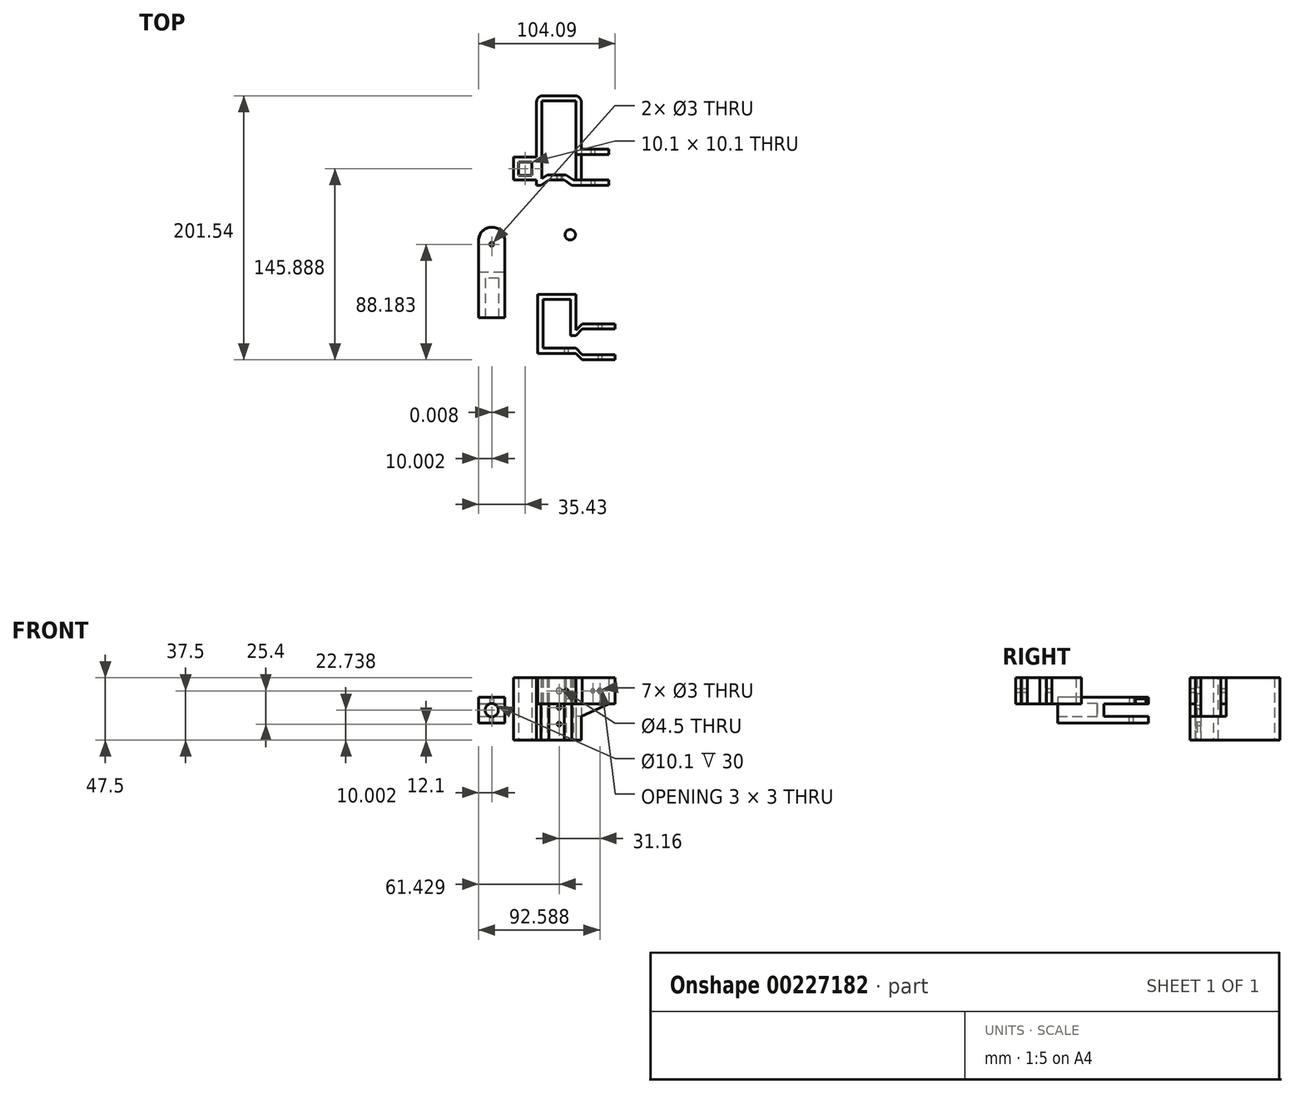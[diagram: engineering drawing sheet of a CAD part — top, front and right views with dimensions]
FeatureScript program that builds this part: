
annotation { "Feature Type Name" : "Feature", "Feature Type Description" : "" }
export const myFeature = defineFeature(function(context is Context, id is Id, definition is map)
    precondition{}
    {
        {
            var Q0;
            Q0=qCreatedBy(makeId("Top.planeOp"),FACE);
            var sketch = newSketch(context, id + "F0", { "sketchPlane" : qUnion([Q0])});
            skLineSegment(sketch, "E0.bottom", {"start": v(-21.91, 56.33) * mm, "end": v(-41.91, 56.33) * mm});
            skLineSegment(sketch, "E1", {"start": v(-21.93, 11.33) * mm, "end": v(-21.93, -13.67) * mm});
            skLineSegment(sketch, "E2.MirrorCS", {"start": v(-41.93, 11.33) * mm, "end": v(-41.93, -13.67) * mm});
            skLineSegment(sketch, "E3", {"start": v(-41.93, 11.33) * mm, "end": v(-21.93, 11.33) * mm});
            skLineSegment(sketch, "E4", {"start": v(-41.93, -13.67) * mm, "end": v(-21.93, -13.67) * mm});
            skLineSegment(sketch, "E5", {"start": v(-31.93, 11.33) * mm, "end": v(-31.91, 56.33) * mm});
            skCircle(sketch, "E6", {"center": v(-31.92, 32.33) * mm, "radius": 1.5 * mm});
            skLineSegment(sketch, "E7", {"start": v(-41.91, 56.33) * mm, "end": v(-41.93, 11.33) * mm});
            skLineSegment(sketch, "E8", {"start": v(-21.91, 56.33) * mm, "end": v(-21.93, 11.33) * mm});
            skLineSegment(sketch, "E9", {"start": v(-41.92, 45.34) * mm, "end": v(-21.92, 45.33) * mm});
            skLineSegment(sketch, "E10", {"start": v(7.2, -37.33) * mm, "end": v(32.2, -37.33) * mm});
            skLineSegment(sketch, "E11", {"start": v(32.2, -37.33) * mm, "end": v(37.16, -32.36) * mm});
            skLineSegment(sketch, "E12", {"start": v(37.16, -32.36) * mm, "end": v(62.16, -32.36) * mm});
            skLineSegment(sketch, "E13", {"start": v(62.16, -32.36) * mm, "end": v(62.16, -42.13) * mm});
            skLineSegment(sketch, "E14", {"start": v(7.2, -37.33) * mm, "end": v(7.2, -42.13) * mm});
            skLineSegment(sketch, "E15", {"start": v(7.2, -42.13) * mm, "end": v(62.16, -42.13) * mm, "construction": true});
            skLineSegment(sketch, "E16.MirrorCS", {"start": v(7.2, -46.93) * mm, "end": v(7.2, -42.13) * mm});
            skLineSegment(sketch, "E17.MirrorCS", {"start": v(7.2, -46.93) * mm, "end": v(32.2, -46.93) * mm});
            skLineSegment(sketch, "E18.MirrorCS", {"start": v(32.2, -46.93) * mm, "end": v(37.16, -51.89) * mm});
            skLineSegment(sketch, "E19.MirrorCS", {"start": v(37.16, -51.89) * mm, "end": v(62.16, -51.89) * mm});
            skLineSegment(sketch, "E20.MirrorCS", {"start": v(62.16, -51.89) * mm, "end": v(62.16, -42.13) * mm});
            skLineSegment(sketch, "E21", {"start": v(3.2, -42.13) * mm, "end": v(3.2, -33.36) * mm});
            skLineSegment(sketch, "E22", {"start": v(3.2, -33.36) * mm, "end": v(32.2, -33.36) * mm});
            skLineSegment(sketch, "E23", {"start": v(32.2, -33.36) * mm, "end": v(37.16, -28.4) * mm});
            skLineSegment(sketch, "E24.MirrorCS", {"start": v(3.2, -42.13) * mm, "end": v(3.2, -50.89) * mm});
            skLineSegment(sketch, "E25.MirrorCS", {"start": v(3.2, -50.89) * mm, "end": v(32.2, -50.89) * mm});
            skLineSegment(sketch, "E26.MirrorCS", {"start": v(32.2, -50.89) * mm, "end": v(37.16, -55.85) * mm});
            skLineSegment(sketch, "E27", {"start": v(62.16, -28.4) * mm, "end": v(62.16, -55.85) * mm});
            skLineSegment(sketch, "E28", {"start": v(37.16, -28.4) * mm, "end": v(62.16, -28.4) * mm});
            skLineSegment(sketch, "E29", {"start": v(37.16, -55.85) * mm, "end": v(62.16, -55.85) * mm});
            skLineSegment(sketch, "E30", {"start": v(3.2, -5.78) * mm, "end": v(3.2, -33.36) * mm});
            skLineSegment(sketch, "E31", {"start": v(7.2, -33.36) * mm, "end": v(7.2, -9.78) * mm});
            skLineSegment(sketch, "E32", {"start": v(7.2, -37.33) * mm, "end": v(7.2, -33.36) * mm});
            skLineSegment(sketch, "E33", {"start": v(32.2, -33.36) * mm, "end": v(32.2, -9.78) * mm});
            skLineSegment(sketch, "E34", {"start": v(28.2, -37.33) * mm, "end": v(28.2, -9.78) * mm});
            skLineSegment(sketch, "E35", {"start": v(7.2, -9.78) * mm, "end": v(32.2, -9.78) * mm});
            skLineSegment(sketch, "E36", {"start": v(32.2, -9.78) * mm, "end": v(32.2, -5.78) * mm});
            skLineSegment(sketch, "E37", {"start": v(3.2, -5.78) * mm, "end": v(32.2, -5.78) * mm});
            skLineSegment(sketch, "E38.MirrorCS", {"start": v(6.25, 85.29) * mm, "end": v(24.75, 85.29) * mm});
            skLineSegment(sketch, "E39", {"start": v(57.44, 104.81) * mm, "end": v(57.44, 77.29) * mm});
            skLineSegment(sketch, "E40", {"start": v(2.25, 81.29) * mm, "end": v(2.25, 145.69) * mm});
            skLineSegment(sketch, "E41", {"start": v(6.25, 85.29) * mm, "end": v(6.25, 141.69) * mm});
            skLineSegment(sketch, "E42", {"start": v(2.25, 81.29) * mm, "end": v(57.44, 81.29) * mm});
            skLineSegment(sketch, "E43", {"start": v(57.44, 77.29) * mm, "end": v(29.27, 77.29) * mm});
            skLineSegment(sketch, "E44", {"start": v(29.27, 77.29) * mm, "end": v(23.5, 81.29) * mm});
            skLineSegment(sketch, "E45", {"start": v(57.44, 91.05) * mm, "end": v(6.25, 91.05) * mm, "construction": true});
            skLineSegment(sketch, "E46", {"start": v(24.75, 85.29) * mm, "end": v(30.52, 81.29) * mm});
            skLineSegment(sketch, "E47", {"start": v(36.44, 104.81) * mm, "end": v(36.44, 145.69) * mm});
            skLineSegment(sketch, "E48", {"start": v(32.44, 100.81) * mm, "end": v(57.44, 100.81) * mm});
            skLineSegment(sketch, "E49", {"start": v(36.44, 104.81) * mm, "end": v(57.44, 104.81) * mm});
            skLineSegment(sketch, "E50", {"start": v(32.44, 100.81) * mm, "end": v(32.44, 141.69) * mm});
            skLineSegment(sketch, "E51", {"start": v(6.25, 141.69) * mm, "end": v(32.44, 141.69) * mm});
            skLineSegment(sketch, "E52", {"start": v(2.25, 145.69) * mm, "end": v(36.44, 145.69) * mm});
            skLineSegment(sketch, "E53", {"start": v(32.8, 81.29) * mm, "end": v(32.8, 77.29) * mm});
            skLineSegment(sketch, "E54", {"start": v(17.52, 85.29) * mm, "end": v(17.52, 81.29) * mm});
            skLineSegment(sketch, "E55.MirrorCS", {"start": v(10.3, 85.29) * mm, "end": v(4.53, 81.29) * mm});
            skLineSegment(sketch, "E56.MirrorCS", {"start": v(5.78, 77.29) * mm, "end": v(11.55, 81.29) * mm});
            skLineSegment(sketch, "E57.MirrorCS", {"start": v(2.25, 81.29) * mm, "end": v(2.25, 77.29) * mm});
            skLineSegment(sketch, "E58", {"start": v(5.78, 77.29) * mm, "end": v(2.25, 77.29) * mm});
            skLineSegment(sketch, "E59", {"start": v(6.25, 85.29) * mm, "end": v(6.25, 82.48) * mm});
            skSolve(sketch);
        }
        {
            var Q0;
            {var subQ2=sQuery(id+"F0.wireOp",EDGE,"CtE1QIkq-5tvS-lQmr-TLQE-PiAnWp6S8LlF");Q0=makeQuery(id+"F0.imprint","IMPRINT",FACE,{"disambiguationData":[TD([[makeQuery(id+"F0.imprint","IMPRINT",EDGE,{"derivedFrom":subQ2}),-1.0]])]});}
            var Q1;
            Q1=makeQuery(id+"F0.imprint","IMPRINT",FACE,{"disambiguationData":[TD([[makeQuery(id+"F0.imprint","IMPRINT",EDGE,{"derivedFrom":sQuery(id+"F0.wireOp",EDGE,"z6zBslmh-39Nm-7tGN-vX3i-qFsrJANIcQPB")}),-1.0]])]});
            var Q2;
            {var subQ2=sQuery(id+"F0.wireOp",EDGE,"9d48ba60-b61e-4945-9312-984ca757d42b0.MirrorCS");Q2=makeQuery(id+"F0.imprint","IMPRINT",FACE,{"disambiguationData":[TD([[makeQuery(id+"F0.imprint","IMPRINT",EDGE,{"derivedFrom":subQ2}),1.0]])]});}
            var Q3;
            {var subQ4=sQuery(id+"F0.wireOp",EDGE,"E1");Q3=makeQuery(id+"F0.imprint","IMPRINT",FACE,{"disambiguationData":[TD([[makeQuery(id+"F0.imprint","IMPRINT",EDGE,{"derivedFrom":subQ4}),-1.0]])]});}
            var Q4;
            {var subQ0=sQuery(id+"F0.wireOp",EDGE,"CtE1QIkq-5tvS-lQmr-TLQE-PiAnWp6S8LlF");Q4=makeQuery(id+"F0.imprint","IMPRINT",FACE,{"disambiguationData":[TD([[makeQuery(id+"F0.imprint","IMPRINT",EDGE,{"derivedFrom":subQ0}),1.0]])]});}
            var Q5;
            {var subQ4=sQuery(id+"F0.wireOp",EDGE,"daFnesJ6-epaf-a9xK-2GaG-miObHF0AM3f9");Q5=makeQuery(id+"F0.imprint","IMPRINT",FACE,{"disambiguationData":[TD([[makeQuery(id+"F0.imprint","IMPRINT",EDGE,{"derivedFrom":subQ4}),1.0]])]});}
            var Q6;
            {var subQ8=sQuery(id+"F0.wireOp",EDGE,"E8");var subQ10=makeQuery(id+"F0.imprint","IMPRINT",VERTEX,{"derivedFrom":subQ8});Q6=makeQuery(id+"F0.imprint","IMPRINT",FACE,{"disambiguationData":[TD([[makeQuery(id+"F0.imprint","IMPRINT",EDGE,{"disambiguationData":[TD([[subQ10,1.0]])],"derivedFrom":subQ8}),-1.0]])]});}
            var Q7;
            {var subQ10=sQuery(id+"F0.wireOp",EDGE,"c9a6f07b-14d8-4156-a2d3-0b1aa78cce260.MirrorCS");Q7=makeQuery(id+"F0.imprint","IMPRINT",FACE,{"disambiguationData":[TD([[makeQuery(id+"F0.imprint","IMPRINT",EDGE,{"derivedFrom":subQ10}),-1.0]])]});}
            var Q8;
            {var subQ1=sQuery(id+"F0.wireOp",EDGE,"E5");var subQ4=sQuery(id+"F0.wireOp",EDGE,"E3");var subQ5=makeQuery(id+"F0.imprint","INTERSECT",VERTEX,{"derivedFrom":[subQ4,subQ1]});Q8=makeQuery(id+"F0.imprint","IMPRINT",FACE,{"disambiguationData":[TD([[makeQuery(id+"F0.imprint","IMPRINT",EDGE,{"disambiguationData":[TD([[subQ5,-1.0]])],"derivedFrom":subQ1}),1.0]])]});}
            var Q9;
            {var subQ1=sQuery(id+"F0.wireOp",EDGE,"E5");var subQ6=sQuery(id+"F0.wireOp",EDGE,"E3");var subQ7=makeQuery(id+"F0.imprint","INTERSECT",VERTEX,{"derivedFrom":[subQ6,subQ1]});Q9=makeQuery(id+"F0.imprint","IMPRINT",FACE,{"disambiguationData":[TD([[makeQuery(id+"F0.imprint","IMPRINT",EDGE,{"disambiguationData":[TD([[subQ7,-1.0]])],"derivedFrom":subQ1}),-1.0]])]});}
            var Q10;
            Q10 = qSketchRegion(id + "F3", true);
            var Q11;
            Q11=makeQuery(id+"F0.imprint","IMPRINT",FACE,{"disambiguationData":[TD([[makeQuery(id+"F0.imprint","IMPRINT",EDGE,{"derivedFrom":sQuery(id+"F0.wireOp",EDGE,"1Q1dtNkS-BfXF-qmHB-TxVw-7IoFosjgP5cW.bottom")}),-1.0]])]});
            extrude(context, id + "F1", {"entities" : qUnion([Q0, Q1, Q2, Q3, Q4, Q5, Q6, Q7, Q8, Q9, Q10, Q11]), "depth" : 5 * mm, "offsetDistance" : 25 * mm});
        }
        {
            var Q0;
            Q0=makeQuery(id+"F1.opExtrude","SWEPT_EDGE",EDGE,{"disambiguationData":[OSD([sQuery(id+"F0.wireOp",EDGE,"E9"),sQuery(id+"F0.wireOp",EDGE,"c9a6f07b-14d8-4156-a2d3-0b1aa78cce260.MirrorCS")])]});
            var Q1;
            Q1=makeQuery(id+"F1.opExtrude","SWEPT_EDGE",EDGE,{"disambiguationData":[OSD([sQuery(id+"F0.wireOp",EDGE,"E8"),sQuery(id+"F0.wireOp",EDGE,"c9a6f07b-14d8-4156-a2d3-0b1aa78cce260.MirrorCS")])]});
            var Q2;
            Q2=makeQuery(id+"F1.opExtrude","SWEPT_EDGE",EDGE,{"disambiguationData":[OSD([sQuery(id+"F0.wireOp",EDGE,"E9"),sQuery(id+"F0.wireOp",EDGE,"daFnesJ6-epaf-a9xK-2GaG-miObHF0AM3f9")])]});
            var Q3;
            Q3=makeQuery(id+"F1.opExtrude","SWEPT_EDGE",EDGE,{"disambiguationData":[OSD([sQuery(id+"F0.wireOp",EDGE,"E7"),sQuery(id+"F0.wireOp",EDGE,"daFnesJ6-epaf-a9xK-2GaG-miObHF0AM3f9")])]});
            fillet(context, id + "F2", {"entities" : qUnion([Q0, Q1, Q2, Q3]), "radius" : 10 * mm, "tangentPropagation" : true, "allowEdgeOverflow" : false});
        }
        {
            var Q0;
            Q0=makeQuery(id+"F1.opExtrude","CAP_FACE",FACE,{"disambiguationData":[OSD([sQuery(id+"F0.wireOp",EDGE,"E0.bottom"),sQuery(id+"F0.wireOp",EDGE,"E1"),sQuery(id+"F0.wireOp",EDGE,"E2.MirrorCS"),sQuery(id+"F0.wireOp",EDGE,"E4"),sQuery(id+"F0.wireOp",EDGE,"E6"),sQuery(id+"F0.wireOp",EDGE,"E7"),sQuery(id+"F0.wireOp",EDGE,"E8")])],"isStart":true});
            var sketch = newSketch(context, id + "F3", { "sketchPlane" : qUnion([Q0])});
            skLineSegment(sketch, "E60", {"start": v(-41.93, -11.33) * mm, "end": v(-21.93, -11.33) * mm});
            skSolve(sketch);
        }
        {
            var Q0;
            Q0=makeQuery(id+"F3.imprint","IMPRINT",FACE,{"disambiguationData":[TD([[makeQuery(id+"F3.imprint","IMPRINT",EDGE,{"derivedFrom":sQuery(id+"F3.wireOp",EDGE,"E60")}),1.0]])]});
            extrude(context, id + "F4", {"entities" : qUnion([Q0]), "operationType" : NewBodyOperationType.ADD, "depth" : 9.53 * mm, "offsetDistance" : 25 * mm});
        }
        {
            var Q0;
            Q0=makeQuery(id+"F4.opExtrude","CAP_FACE",FACE,{"disambiguationData":[OSD([sQuery(id+"F0.wireOp",EDGE,"E1"),sQuery(id+"F0.wireOp",EDGE,"E2.MirrorCS"),sQuery(id+"F0.wireOp",EDGE,"E4"),sQuery(id+"F3.wireOp",EDGE,"E60")])],"isStart":false});
            var sketch = newSketch(context, id + "F5", { "sketchPlane" : qUnion([Q0])});
            skLineSegment(sketch, "E61.bottom", {"start": v(-21.93, 13.67) * mm, "end": v(-41.93, 13.67) * mm});
            skLineSegment(sketch, "E61.top", {"start": v(-21.93, -56.33) * mm, "end": v(-41.93, -56.33) * mm});
            skLineSegment(sketch, "E61.left", {"start": v(-21.93, 13.67) * mm, "end": v(-21.93, -56.33) * mm});
            skLineSegment(sketch, "E61.right", {"start": v(-41.93, 13.67) * mm, "end": v(-41.93, -56.33) * mm});
            skLineSegment(sketch, "E62", {"start": v(-21.93, -11.33) * mm, "end": v(-41.93, -11.33) * mm, "construction": true});
            skCircle(sketch, "E63", {"center": v(-31.93, -32.33) * mm, "radius": 1.5 * mm});
            skPoint(sketch, "E63.centerSnap0", {"position": v(-31.93, -11.33) * mm});
            skLineSegment(sketch, "E64", {"start": v(-21.93, -45.33) * mm, "end": v(-41.93, -45.33) * mm});
            skLineSegment(sketch, "E65", {"start": v(-31.93, -45.33) * mm, "end": v(-31.93, -11.33) * mm, "construction": true});
            skSolve(sketch);
        }
        {
            var Q0;
            {var subQ0=sQuery(id+"F5.wireOp",EDGE,"E61.bottom");Q0=makeQuery(id+"F5.imprint","IMPRINT",FACE,{"disambiguationData":[TD([[makeQuery(id+"F5.imprint","IMPRINT",EDGE,{"derivedFrom":subQ0}),1.0]])]});}
            var Q1;
            {var subQ0=sQuery(id+"F5.wireOp",EDGE,"E62");Q1=makeQuery(id+"F5.imprint","IMPRINT",FACE,{"disambiguationData":[TD([[makeQuery(id+"F5.imprint","IMPRINT",EDGE,{"derivedFrom":subQ0}),-1.0]])]});}
            var Q2;
            Q2=makeQuery(id+"F5.imprint","IMPRINT",FACE,{"disambiguationData":[TD([[makeQuery(id+"F5.imprint","IMPRINT",EDGE,{"derivedFrom":sQuery(id+"F5.wireOp",EDGE,"E63")}),-1.0]])]});
            var Q3;
            {var subQ0=sQuery(id+"F5.wireOp",EDGE,"E61.bottom");Q3=makeQuery(id+"F5.imprint","IMPRINT",FACE,{"disambiguationData":[TD([[makeQuery(id+"F5.imprint","IMPRINT",EDGE,{"derivedFrom":subQ0}),-1.0]])]});}
            extrude(context, id + "F6", {"entities" : qUnion([Q0, Q1, Q2, Q3]), "operationType" : NewBodyOperationType.ADD, "depth" : 5 * mm, "offsetDistance" : 25 * mm});
        }
        {
            var Q0;
            Q0=makeQuery(id+"F6.opExtrude","SWEPT_EDGE",EDGE,{"disambiguationData":[OSD([sQuery(id+"F5.wireOp",EDGE,"E61.right"),sQuery(id+"F5.wireOp",EDGE,"E64")])]});
            var Q1;
            Q1=makeQuery(id+"F6.opExtrude","SWEPT_EDGE",EDGE,{"disambiguationData":[OSD([sQuery(id+"F5.wireOp",EDGE,"E61.left"),sQuery(id+"F5.wireOp",EDGE,"E64")])]});
            fillet(context, id + "F7", {"entities" : qUnion([Q0, Q1]), "radius" : 10 * mm, "tangentPropagation" : true, "allowEdgeOverflow" : false});
        }
        {
            var Q0;
            {var subQ0=sQuery(id+"F0.wireOp",EDGE,"E4");Q0=makeQuery(id+"F4.boolean.opBoolean","MERGE",FACE,{"derivedFrom":[makeQuery(id+"F1.opExtrude","SWEPT_FACE",FACE,{"disambiguationData":[OSD([subQ0])]}),makeQuery(id+"F4.opExtrude","SWEPT_FACE",FACE,{"disambiguationData":[OSD([subQ0])]})]});}
            var sketch = newSketch(context, id + "F8", { "sketchPlane" : qUnion([Q0])});
            skCircle(sketch, "E66", {"center": v(-31.93, -4.76) * mm, "radius": 5.05 * mm});
            skPoint(sketch, "E66.centerSnap0", {"position": v(-31.93, 5) * mm});
            skSolve(sketch);
        }
        {
            var Q0;
            Q0=makeQuery(id+"F0.imprint","IMPRINT",FACE,{"disambiguationData":[TD([[makeQuery(id+"F0.imprint","IMPRINT",EDGE,{"derivedFrom":sQuery(id+"F0.wireOp",EDGE,"E14")}),-1.0]])]});
            var Q1;
            {var subQ0=sQuery(id+"F0.wireOp",EDGE,"E30");Q1=makeQuery(id+"F0.imprint","IMPRINT",FACE,{"disambiguationData":[TD([[makeQuery(id+"F0.imprint","IMPRINT",EDGE,{"derivedFrom":subQ0}),1.0]])]});}
            var Q2;
            {var subQ0=sQuery(id+"F0.wireOp",EDGE,"E12");Q2=makeQuery(id+"F0.imprint","IMPRINT",FACE,{"disambiguationData":[TD([[makeQuery(id+"F0.imprint","IMPRINT",EDGE,{"derivedFrom":subQ0}),1.0]])]});}
            var Q3;
            {var subQ3=sQuery(id+"F0.wireOp",EDGE,"XBbEQiE6-Z9xt-ZPnH-mPWf-PrI6pPlz04wO");Q3=makeQuery(id+"F0.imprint","IMPRINT",FACE,{"disambiguationData":[TD([[makeQuery(id+"F0.imprint","IMPRINT",EDGE,{"derivedFrom":subQ3}),-1.0]])]});}
            var Q4;
            {var subQ0=sQuery(id+"F0.wireOp",EDGE,"E33");Q4=makeQuery(id+"F0.imprint","IMPRINT",FACE,{"disambiguationData":[TD([[makeQuery(id+"F0.imprint","IMPRINT",EDGE,{"derivedFrom":subQ0}),1.0]])]});}
            var Q5;
            {var subQ1=sQuery(id+"F0.wireOp",EDGE,"72db4730-2340-4a1c-bc84-b23054559dcc");Q5=makeQuery(id+"F0.imprint","IMPRINT",FACE,{"disambiguationData":[TD([[makeQuery(id+"F0.imprint","IMPRINT",EDGE,{"derivedFrom":subQ1}),1.0]])]});}
            var Q6;
            Q6=makeQuery(id+"F0.imprint","IMPRINT",FACE,{"disambiguationData":[TD([[makeQuery(id+"F0.imprint","IMPRINT",EDGE,{"derivedFrom":sQuery(id+"F0.wireOp",EDGE,"d60c7e22-afe8-4185-99c7-5cb7434f99d0")}),-1.0]])]});
            var Q7;
            {var subQ0=sQuery(id+"F0.wireOp",EDGE,"E43");Q7=makeQuery(id+"F0.imprint","IMPRINT",FACE,{"disambiguationData":[TD([[makeQuery(id+"F0.imprint","IMPRINT",EDGE,{"derivedFrom":subQ0}),-1.0]])]});}
            var Q8;
            {var subQ0=sQuery(id+"F0.wireOp",EDGE,"CSoZNY7o-y4bp-1TmG-7ssV-1xZfQapDGbnf");Q8=makeQuery(id+"F0.imprint","IMPRINT",FACE,{"disambiguationData":[TD([[makeQuery(id+"F0.imprint","IMPRINT",EDGE,{"derivedFrom":subQ0}),-1.0]])]});}
            var Q9;
            {var subQ3=sQuery(id+"F0.wireOp",EDGE,"uGOKfyWa-nkCR-v7qt-ErlA-4CgWz3QyV5Tk");Q9=makeQuery(id+"F0.imprint","IMPRINT",FACE,{"disambiguationData":[TD([[makeQuery(id+"F0.imprint","IMPRINT",EDGE,{"derivedFrom":subQ3}),1.0]])]});}
            var Q10;
            {var subQ0=sQuery(id+"F0.wireOp",EDGE,"E44");Q10=makeQuery(id+"F0.imprint","IMPRINT",FACE,{"disambiguationData":[TD([[makeQuery(id+"F0.imprint","IMPRINT",EDGE,{"derivedFrom":subQ0}),-1.0]])]});}
            var Q11;
            {var subQ2=sQuery(id+"F0.wireOp",EDGE,"E40");Q11=makeQuery(id+"F0.imprint","IMPRINT",FACE,{"disambiguationData":[TD([[makeQuery(id+"F0.imprint","IMPRINT",EDGE,{"derivedFrom":subQ2}),-1.0]])]});}
            var Q12;
            {var subQ2=sQuery(id+"F0.wireOp",EDGE,"8fHTCkTu-zAOj-TMkr-ZO5F-SEi9VVDEdafV");Q12=makeQuery(id+"F0.imprint","IMPRINT",FACE,{"disambiguationData":[TD([[makeQuery(id+"F0.imprint","IMPRINT",EDGE,{"derivedFrom":subQ2}),-1.0]])]});}
            var Q13;
            {var subQ3=sQuery(id+"F0.wireOp",EDGE,"E56.MirrorCS");Q13=makeQuery(id+"F0.imprint","IMPRINT",FACE,{"disambiguationData":[TD([[makeQuery(id+"F0.imprint","IMPRINT",EDGE,{"derivedFrom":subQ3}),1.0]])]});}
            var Q14;
            {var subQ0=sQuery(id+"F0.wireOp",EDGE,"E54");Q14=makeQuery(id+"F0.imprint","IMPRINT",FACE,{"disambiguationData":[TD([[makeQuery(id+"F0.imprint","IMPRINT",EDGE,{"derivedFrom":subQ0}),-1.0]])]});}
            var Q15;
            {var subQ0=sQuery(id+"F0.wireOp",EDGE,"E46");Q15=makeQuery(id+"F0.imprint","IMPRINT",FACE,{"disambiguationData":[TD([[makeQuery(id+"F0.imprint","IMPRINT",EDGE,{"derivedFrom":subQ0}),-1.0]])]});}
            extrude(context, id + "F9", {"entities" : qUnion([Q0, Q1, Q2, Q3, Q4, Q5, Q6, Q7, Q8, Q9, Q10, Q11, Q12, Q13, Q14, Q15]), "depth" : 20 * mm, "offsetDistance" : 25 * mm});
        }
        {
            var Q0;
            Q0=makeQuery(id+"F9.opExtrude","SWEPT_FACE",FACE,{"disambiguationData":[OSD([sQuery(id+"F0.wireOp",EDGE,"E29")])]});
            var sketch = newSketch(context, id + "F10", { "sketchPlane" : qUnion([Q0])});
            skCircle(sketch, "E67", {"center": v(50.66, 10) * mm, "radius": 1.5 * mm});
            skPoint(sketch, "E67.centerSnap0", {"position": v(37.16, 10) * mm});
            skSolve(sketch);
        }
        {
            var Q0;
            Q0=makeQuery(id+"F9.opExtrude","SWEPT_FACE",FACE,{"disambiguationData":[OSD([sQuery(id+"F0.wireOp",EDGE,"E25.MirrorCS")])]});
            var sketch = newSketch(context, id + "F11", { "sketchPlane" : qUnion([Q0])});
            skPoint(sketch, "E68.centerSnap0", {"position": v(32.2, 10) * mm});
            skPoint(sketch, "E68.centerSnap1", {"position": v(17.7, 20) * mm});
            skCircle(sketch, "E69", {"center": v(24.9, 10) * mm, "radius": 1.5 * mm});
            skSolve(sketch);
        }
        {
            var Q0;
            Q0=makeQuery(id+"F11.imprint","IMPRINT",FACE,{"disambiguationData":[TD([[makeQuery(id+"F11.imprint","IMPRINT",EDGE,{"derivedFrom":sQuery(id+"F11.wireOp",EDGE,"E68")}),1.0]])]});
            var Q1;
            Q1=makeQuery(id+"F11.imprint","IMPRINT",FACE,{"disambiguationData":[TD([[makeQuery(id+"F11.imprint","IMPRINT",EDGE,{"derivedFrom":sQuery(id+"F11.wireOp",EDGE,"E69")}),1.0]])]});
            extrude(context, id + "F12", {"entities" : qUnion([Q0, Q1]), "operationType" : NewBodyOperationType.REMOVE, "oppositeDirection" : true, "depth" : 25 * mm, "offsetDistance" : 25 * mm});
        }
        {
            var Q0;
            Q0=makeQuery(id+"F10.imprint","IMPRINT",FACE,{"disambiguationData":[TD([[makeQuery(id+"F10.imprint","IMPRINT",EDGE,{"derivedFrom":sQuery(id+"F10.wireOp",EDGE,"Pd4Yzp6c-uVQW-pqn9-VgG2-u9d980DHV2Mr")}),1.0]])]});
            var Q1;
            Q1=makeQuery(id+"F10.imprint","IMPRINT",FACE,{"disambiguationData":[TD([[makeQuery(id+"F10.imprint","IMPRINT",EDGE,{"derivedFrom":sQuery(id+"F10.wireOp",EDGE,"ebFhJDeN-R1jm-PNRe-eJwy-XtfoPDOoVAFP")}),1.0]])]});
            var Q2;
            Q2=makeQuery(id+"F10.imprint","IMPRINT",FACE,{"disambiguationData":[TD([[makeQuery(id+"F10.imprint","IMPRINT",EDGE,{"derivedFrom":sQuery(id+"F10.wireOp",EDGE,"E67")}),1.0]])]});
            extrude(context, id + "F13", {"entities" : qUnion([Q0, Q1, Q2]), "operationType" : NewBodyOperationType.REMOVE, "oppositeDirection" : true, "depth" : 35 * mm, "offsetDistance" : 25 * mm});
        }
        {
            var Q0;
            Q0=makeQuery(id+"F8.imprint","IMPRINT",FACE,{"disambiguationData":[TD([[makeQuery(id+"F8.imprint","IMPRINT",EDGE,{"derivedFrom":sQuery(id+"F8.wireOp",EDGE,"E66")}),1.0]])]});
            extrude(context, id + "F14", {"entities" : qUnion([Q0]), "operationType" : NewBodyOperationType.REMOVE, "oppositeDirection" : true, "depth" : 20 * mm, "offsetDistance" : 25 * mm});
        }
        {
            var Q0;
            {var subQ0=sQuery(id+"F0.wireOp",EDGE,"E42");Q0=makeQuery(id+"F9.opExtrude","SWEPT_FACE",FACE,{"disambiguationData":[OSD([subQ0]),TDD([makeQuery(id+"F0.imprint","IMPRINT",EDGE,{"disambiguationData":[TD([[makeQuery(id+"F0.imprint","INTERSECT",VERTEX,{"derivedFrom":[subQ0,sQuery(id+"F0.wireOp",EDGE,"E44")]}),1.0]])],"derivedFrom":subQ0})])]});}
            var sketch = newSketch(context, id + "F15", { "sketchPlane" : qUnion([Q0])});
            skCircle(sketch, "E70", {"center": v(19.5, 10) * mm, "radius": 2.25 * mm});
            skCircle(sketch, "E71", {"center": v(19.5, -2.7) * mm, "radius": 1.5 * mm});
            skCircle(sketch, "E72", {"center": v(19.5, -15.4) * mm, "radius": 1.5 * mm});
            skSolve(sketch);
        }
        {
            var Q0;
            Q0=makeQuery(id+"F15.imprint","IMPRINT",FACE,{"disambiguationData":[TD([[makeQuery(id+"F15.imprint","IMPRINT",EDGE,{"derivedFrom":sQuery(id+"F15.wireOp",EDGE,"E72")}),1.0]])]});
            var Q1;
            Q1=makeQuery(id+"F15.imprint","IMPRINT",FACE,{"disambiguationData":[TD([[makeQuery(id+"F15.imprint","IMPRINT",EDGE,{"derivedFrom":sQuery(id+"F15.wireOp",EDGE,"E71")}),1.0]])]});
            var Q2;
            Q2=makeQuery(id+"F15.imprint","IMPRINT",FACE,{"disambiguationData":[TD([[makeQuery(id+"F15.imprint","IMPRINT",EDGE,{"derivedFrom":sQuery(id+"F15.wireOp",EDGE,"E70")}),1.0]])]});
            extrude(context, id + "F16", {"entities" : qUnion([Q0, Q1, Q2]), "operationType" : NewBodyOperationType.REMOVE, "oppositeDirection" : true, "depth" : 25 * mm, "offsetDistance" : 25 * mm});
        }
        {
            var Q0;
            Q0=makeQuery(id+"F9.opExtrude","SWEPT_FACE",FACE,{"disambiguationData":[OSD([sQuery(id+"F0.wireOp",EDGE,"E43")])]});
            var sketch = newSketch(context, id + "F17", { "sketchPlane" : qUnion([Q0])});
            skCircle(sketch, "E73", {"center": v(45.19, 10) * mm, "radius": 1.5 * mm});
            skSolve(sketch);
        }
        {
            var Q0;
            Q0 = qSketchRegion(id + "F17", true);
            extrude(context, id + "F18", {"entities" : qUnion([Q0]), "operationType" : NewBodyOperationType.REMOVE, "oppositeDirection" : true, "depth" : 35 * mm, "offsetDistance" : 25 * mm});
        }
        {
            var Q0;
            {var subQ0=sQuery(id+"F0.wireOp",EDGE,"E44");Q0=makeQuery(id+"F0.imprint","IMPRINT",FACE,{"disambiguationData":[TD([[makeQuery(id+"F0.imprint","IMPRINT",EDGE,{"derivedFrom":subQ0}),-1.0]])]});}
            var Q1;
            {var subQ2=sQuery(id+"F0.wireOp",EDGE,"8fHTCkTu-zAOj-TMkr-ZO5F-SEi9VVDEdafV");Q1=makeQuery(id+"F0.imprint","IMPRINT",FACE,{"disambiguationData":[TD([[makeQuery(id+"F0.imprint","IMPRINT",EDGE,{"derivedFrom":subQ2}),-1.0]])]});}
            var Q2;
            {var subQ0=sQuery(id+"F0.wireOp",EDGE,"E54");Q2=makeQuery(id+"F0.imprint","IMPRINT",FACE,{"disambiguationData":[TD([[makeQuery(id+"F0.imprint","IMPRINT",EDGE,{"derivedFrom":subQ0}),-1.0]])]});}
            var Q3;
            {var subQ0=sQuery(id+"F0.wireOp",EDGE,"E46");Q3=makeQuery(id+"F0.imprint","IMPRINT",FACE,{"disambiguationData":[TD([[makeQuery(id+"F0.imprint","IMPRINT",EDGE,{"derivedFrom":subQ0}),-1.0]])]});}
            var Q4;
            {var subQ4=sQuery(id+"F0.wireOp",EDGE,"E40");Q4=makeQuery(id+"F0.imprint","IMPRINT",FACE,{"disambiguationData":[TD([[makeQuery(id+"F0.imprint","IMPRINT",EDGE,{"derivedFrom":subQ4}),-1.0]])]});}
            var Q5;
            {var subQ3=sQuery(id+"F0.wireOp",EDGE,"E56.MirrorCS");Q5=makeQuery(id+"F0.imprint","IMPRINT",FACE,{"disambiguationData":[TD([[makeQuery(id+"F0.imprint","IMPRINT",EDGE,{"derivedFrom":subQ3}),1.0]])]});}
            extrude(context, id + "F19", {"entities" : qUnion([Q0, Q1, Q2, Q3, Q4, Q5]), "operationType" : NewBodyOperationType.ADD, "oppositeDirection" : true, "depth" : 27.5 * mm, "offsetDistance" : 25 * mm});
        }
        {
            var Q0;
            {var subQ0=sQuery(id+"F0.wireOp",EDGE,"E48");Q0=makeQuery(id+"F19.boolean.opBoolean","MERGE",FACE,{"derivedFrom":[makeQuery(id+"F9.opExtrude","SWEPT_FACE",FACE,{"disambiguationData":[OSD([subQ0])]}),makeQuery(id+"F19.opExtrude","SWEPT_FACE",FACE,{"disambiguationData":[OSD([subQ0])]})]});}
            var sketch = newSketch(context, id + "F20", { "sketchPlane" : qUnion([Q0])});
            skLineSegment(sketch, "E74", {"start": v(36.44, -27.5) * mm, "end": v(36.44, -9.5) * mm});
            skLineSegment(sketch, "E75", {"start": v(36.44, -9.5) * mm, "end": v(32.44, -9.5) * mm});
            skSolve(sketch);
        }
        {
            var Q0;
            {var subQ0=sQuery(id+"F20.wireOp",EDGE,"E74");Q0=makeQuery(id+"F20.imprint","IMPRINT",FACE,{"disambiguationData":[TD([[makeQuery(id+"F20.imprint","IMPRINT",EDGE,{"derivedFrom":subQ0}),1.0]])]});}
            extrude(context, id + "F21", {"entities" : qUnion([Q0]), "operationType" : NewBodyOperationType.ADD, "depth" : 23.52 * mm, "offsetDistance" : 25 * mm});
        }
        {
            var Q0;
            Q0=makeQuery(id+"F15.imprint","IMPRINT",FACE,{"disambiguationData":[TD([[makeQuery(id+"F15.imprint","IMPRINT",EDGE,{"derivedFrom":sQuery(id+"F15.wireOp",EDGE,"E72")}),1.0]])]});
            var Q1;
            Q1=makeQuery(id+"F15.imprint","IMPRINT",FACE,{"disambiguationData":[TD([[makeQuery(id+"F15.imprint","IMPRINT",EDGE,{"derivedFrom":sQuery(id+"F15.wireOp",EDGE,"E71")}),1.0]])]});
            extrude(context, id + "F22", {"entities" : qUnion([Q0, Q1]), "operationType" : NewBodyOperationType.REMOVE, "oppositeDirection" : true, "depth" : 25 * mm, "offsetDistance" : 25 * mm});
        }
        {
            var Q0;
            {var subQ0=sQuery(id+"F0.wireOp",EDGE,"E43");Q0=makeQuery(id+"F21.boolean.opBoolean","MERGE",FACE,{"derivedFrom":[makeQuery(id+"F19.boolean.opBoolean","MERGE",FACE,{"derivedFrom":[makeQuery(id+"F9.opExtrude","SWEPT_FACE",FACE,{"disambiguationData":[OSD([subQ0])]}),makeQuery(id+"F19.opExtrude","SWEPT_FACE",FACE,{"disambiguationData":[OSD([subQ0])]})]}),makeQuery(id+"F21.opExtrude","CAP_FACE",FACE,{"disambiguationData":[OSD([sQuery(id+"F0.wireOp",EDGE,"E48"),sQuery(id+"F0.wireOp",EDGE,"E50"),sQuery(id+"F20.wireOp",EDGE,"E74"),sQuery(id+"F20.wireOp",EDGE,"E75")])],"isStart":false})]});}
            var sketch = newSketch(context, id + "F23", { "sketchPlane" : qUnion([Q0])});
            skLineSegment(sketch, "E76", {"start": v(36.44, -9.5) * mm, "end": v(57.44, 0) * mm});
            skLineSegment(sketch, "E77", {"start": v(36.44, -27.5) * mm, "end": v(57.44, -27.5) * mm});
            skLineSegment(sketch, "E78", {"start": v(57.44, -27.5) * mm, "end": v(57.44, 0) * mm});
            skSolve(sketch);
        }
        {
            var Q0;
            Q0=makeQuery(id+"F23.imprint","IMPRINT",FACE,{"disambiguationData":[TD([[makeQuery(id+"F23.imprint","IMPRINT",EDGE,{"derivedFrom":sQuery(id+"F23.wireOp",EDGE,"E76")}),1.0]])]});
            extrude(context, id + "F24", {"entities" : qUnion([Q0]), "operationType" : NewBodyOperationType.ADD, "oppositeDirection" : true, "depth" : 4 * mm, "offsetDistance" : 25 * mm});
        }
        {
            var Q0;
            Q0=makeQuery(id+"F23.imprint","IMPRINT",FACE,{"disambiguationData":[TD([[makeQuery(id+"F23.imprint","IMPRINT",EDGE,{"derivedFrom":sQuery(id+"F23.wireOp",EDGE,"E76")}),-1.0]])]});
            extrude(context, id + "F25", {"entities" : qUnion([Q0]), "operationType" : NewBodyOperationType.REMOVE, "oppositeDirection" : true, "depth" : 35 * mm, "offsetDistance" : 25 * mm});
        }
        {
            var Q0;
            {var subQ0=sQuery(id+"F0.wireOp",EDGE,"E52");var subQ1=sQuery(id+"F0.wireOp",EDGE,"E40");Q0=makeQuery(id+"F19.boolean.opBoolean","MERGE",EDGE,{"derivedFrom":[makeQuery(id+"F9.opExtrude","SWEPT_EDGE",EDGE,{"disambiguationData":[OSD([subQ1,subQ0])]}),makeQuery(id+"F19.opExtrude","SWEPT_EDGE",EDGE,{"disambiguationData":[OSD([subQ1,subQ0])]})]});}
            var Q1;
            {var subQ0=sQuery(id+"F0.wireOp",EDGE,"E52");var subQ1=sQuery(id+"F0.wireOp",EDGE,"E47");Q1=makeQuery(id+"F19.boolean.opBoolean","MERGE",EDGE,{"derivedFrom":[makeQuery(id+"F9.opExtrude","SWEPT_EDGE",EDGE,{"disambiguationData":[OSD([subQ1,subQ0])]}),makeQuery(id+"F19.opExtrude","SWEPT_EDGE",EDGE,{"disambiguationData":[OSD([subQ1,subQ0])]})]});}
            fillet(context, id + "F26", {"entities" : qUnion([Q0, Q1]), "radius" : 5 * mm, "tangentPropagation" : true, "allowEdgeOverflow" : false});
        }
        {
            var Q0;
            {var subQ0=sQuery(id+"F0.wireOp",EDGE,"E40");Q0=makeQuery(id+"F19.boolean.opBoolean","MERGE",FACE,{"derivedFrom":[makeQuery(id+"F9.opExtrude","SWEPT_FACE",FACE,{"disambiguationData":[OSD([subQ0])]}),makeQuery(id+"F19.opExtrude","SWEPT_FACE",FACE,{"disambiguationData":[OSD([subQ0])]})]});}
            var sketch = newSketch(context, id + "F27", { "sketchPlane" : qUnion([Q0])});
            skLineSegment(sketch, "E79", {"start": v(-81.29, -27.5) * mm, "end": v(-98.79, -27.5) * mm});
            skLineSegment(sketch, "E80", {"start": v(-98.79, -27.5) * mm, "end": v(-98.79, 20) * mm});
            skLineSegment(sketch, "E81", {"start": v(-98.79, 20) * mm, "end": v(-81.29, 20) * mm});
            skLineSegment(sketch, "E82", {"start": v(-81.29, 20) * mm, "end": v(-81.29, -27.5) * mm});
            skSolve(sketch);
        }
        {
            var Q0;
            Q0=makeQuery(id+"F27.imprint","IMPRINT",FACE,{"disambiguationData":[TD([[makeQuery(id+"F27.imprint","IMPRINT",EDGE,{"derivedFrom":sQuery(id+"F27.wireOp",EDGE,"E79")}),-1.0]])]});
            extrude(context, id + "F28", {"entities" : qUnion([Q0]), "operationType" : NewBodyOperationType.ADD, "depth" : 17.5 * mm, "offsetDistance" : 25 * mm});
        }
        {
            var Q0;
            Q0=makeQuery(id+"F28.opExtrude","SWEPT_FACE",FACE,{"disambiguationData":[OSD([sQuery(id+"F27.wireOp",EDGE,"E79")])]});
            var sketch = newSketch(context, id + "F29", { "sketchPlane" : qUnion([Q0])});
            skLineSegment(sketch, "E83.bottom", {"start": v(-11.55, -84.99) * mm, "end": v(-1.45, -84.99) * mm});
            skLineSegment(sketch, "E83.top", {"start": v(-11.55, -95.09) * mm, "end": v(-1.45, -95.09) * mm});
            skLineSegment(sketch, "E83.left", {"start": v(-11.55, -84.99) * mm, "end": v(-11.55, -95.09) * mm});
            skLineSegment(sketch, "E83.right", {"start": v(-1.45, -84.99) * mm, "end": v(-1.45, -95.09) * mm});
            skPoint(sketch, "E83.middle", {"position": v(-6.5, -90.04) * mm});
            skPoint(sketch, "E83.middle.positionSnap0", {"position": v(-6.5, -98.79) * mm});
            skPoint(sketch, "E83.middle.positionSnap1", {"position": v(-15.25, -90.04) * mm});
            skPoint(sketch, "E83.centerSnap0", {"position": v(-6.5, -98.79) * mm});
            skPoint(sketch, "E83.centerSnap1", {"position": v(-15.25, -90.04) * mm});
            skSolve(sketch);
        }
        {
            var Q0;
            Q0=makeQuery(id+"F29.imprint","IMPRINT",FACE,{"disambiguationData":[TD([[makeQuery(id+"F29.imprint","IMPRINT",EDGE,{"derivedFrom":sQuery(id+"F29.wireOp",EDGE,"E83.bottom")}),-1.0]])]});
            extrude(context, id + "F30", {"entities" : qUnion([Q0]), "operationType" : NewBodyOperationType.REMOVE, "oppositeDirection" : true, "depth" : 50 * mm, "offsetDistance" : 25 * mm});
        }
        {
            var Q0;
            {var subQ0=sQuery(id+"F0.wireOp",EDGE,"E4");Q0=makeQuery(id+"F6.boolean.opBoolean","MERGE",FACE,{"derivedFrom":[makeQuery(id+"F4.boolean.opBoolean","MERGE",FACE,{"derivedFrom":[makeQuery(id+"F1.opExtrude","SWEPT_FACE",FACE,{"disambiguationData":[OSD([subQ0])]}),makeQuery(id+"F4.opExtrude","SWEPT_FACE",FACE,{"disambiguationData":[OSD([subQ0])]})]}),makeQuery(id+"F6.opExtrude","SWEPT_FACE",FACE,{"disambiguationData":[OSD([sQuery(id+"F5.wireOp",EDGE,"E61.bottom")])]})]});}
            extrude(context, id + "F31", {"entities" : qUnion([Q0]), "operationType" : NewBodyOperationType.ADD, "depth" : 10 * mm, "offsetDistance" : 25 * mm});
        }
        {
            var Q0;
            Q0=qCreatedBy(makeId("Top.planeOp"),FACE);
            var sketch = newSketch(context, id + "F32", { "sketchPlane" : qUnion([Q0])});
            skCircle(sketch, "E84", {"center": v(28, 39.6) * mm, "radius": 4 * mm});
            skSolve(sketch);
        }
        {
            var Q0;
            Q0=makeQuery(id+"F32.imprint","IMPRINT",FACE,{"disambiguationData":[TD([[makeQuery(id+"F32.imprint","IMPRINT",EDGE,{"derivedFrom":sQuery(id+"F32.wireOp",EDGE,"E84")}),1.0]])]});
            extrude(context, id + "F33", {"entities" : qUnion([Q0]), "depth" : 3.76 * mm, "offsetDistance" : 25 * mm});
        }
    });
